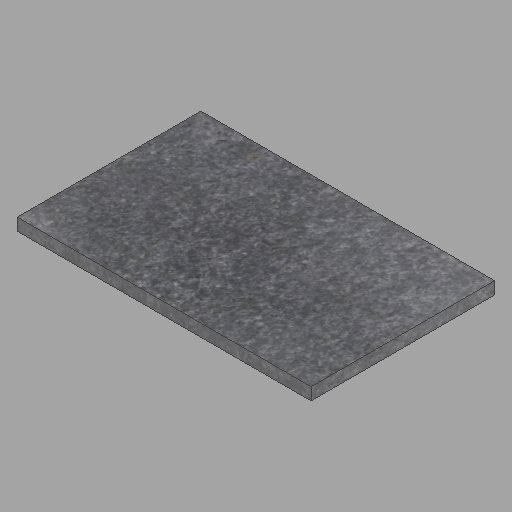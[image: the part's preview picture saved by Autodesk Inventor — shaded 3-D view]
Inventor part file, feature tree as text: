
AUTODESK INVENTOR PART (.ipt)
format: ipt  version: 2023 (Build 270158000, 158)  size: 226,304 bytes
history: native  units: in
note: dims shown in document units (in); Inventor stores cm internally (conversion verified against a paired STEP export)
features: other x1, extrude x1, sketch x1
ambient origin geometry x8: Origin, YZ Plane, XZ Plane, XY Plane, X Axis, Y Axis, Z Axis, Center Point
bodies: Solid1 (feature_tree)
feature tree (3):
  other  "2x30x48-7"
  extrude  "Extrusion1"  Depth=30.0in
  sketch  "Sketch1"  dims[d0=2.0in d1=30.0in d2=48.0in d3=0.0in]
